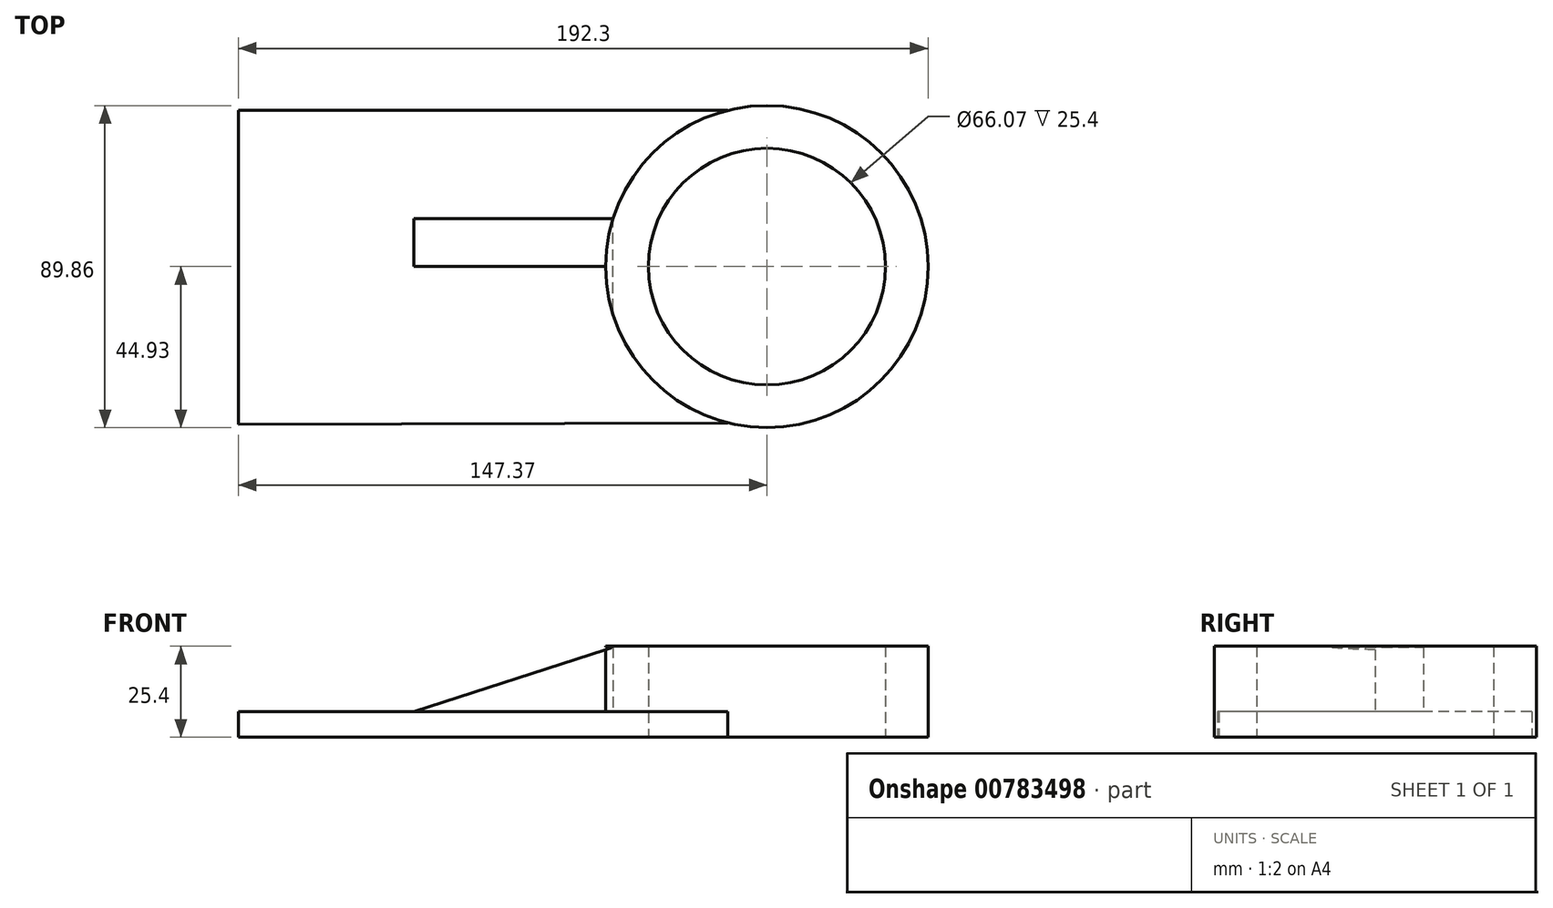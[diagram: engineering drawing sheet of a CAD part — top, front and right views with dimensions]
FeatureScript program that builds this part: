
annotation { "Feature Type Name" : "Feature", "Feature Type Description" : "" }
export const myFeature = defineFeature(function(context is Context, id is Id, definition is map)
    precondition{}
    {
        {
            var Q0;
            Q0=qCreatedBy(makeId("Top.planeOp"),FACE);
            var sketch = newSketch(context, id + "F0", { "sketchPlane" : qUnion([Q0])});
            skCircle(sketch, "E0", {"center": v(0, 0) * mm, "radius": 44.93 * mm});
            skLineSegment(sketch, "E1", {"start": v(-10.88, 43.59) * mm, "end": v(-147.37, 43.59) * mm});
            skLineSegment(sketch, "E2", {"start": v(-147.37, 43.59) * mm, "end": v(-147.37, -43.98) * mm});
            skLineSegment(sketch, "E3", {"start": v(-10.88, -43.59) * mm, "end": v(-147.37, -43.98) * mm});
            skCircle(sketch, "E4", {"center": v(0, 0) * mm, "radius": 33.03 * mm});
            skSolve(sketch);
        }
        {
            var Q0;
            {var subQ0=sQuery(id+"F0.wireOp",EDGE,"w4sub4mG-jCmE-7y8q-nihd-duvU38DYMYJ6");Q0=makeQuery(id+"F0.imprint","IMPRINT",FACE,{"disambiguationData":[TD([[makeQuery(id+"F0.imprint","IMPRINT",EDGE,{"derivedFrom":subQ0}),-1.0]])]});}
            var Q1;
            {var subQ0=sQuery(id+"F0.wireOp",EDGE,"w4sub4mG-jCmE-7y8q-nihd-duvU38DYMYJ6");Q1=makeQuery(id+"F0.imprint","IMPRINT",FACE,{"disambiguationData":[TD([[makeQuery(id+"F0.imprint","IMPRINT",EDGE,{"derivedFrom":subQ0}),1.0]])]});}
            var Q2;
            Q2=makeQuery(id+"F0.imprint","IMPRINT",FACE,{"disambiguationData":[TD([[makeQuery(id+"F0.imprint","IMPRINT",EDGE,{"derivedFrom":sQuery(id+"F0.wireOp",EDGE,"E4")}),-1.0]])]});
            extrude(context, id + "F1", {"entities" : qUnion([Q0, Q1, Q2]), "depth" : 25.4 * mm, "offsetDistance" : 25.4 * mm});
        }
        {
            var Q0;
            Q0 = qSketchRegion(id + "F0", true);
            extrude(context, id + "F2", {"entities" : qUnion([Q0]), "operationType" : NewBodyOperationType.ADD, "depth" : 7.11 * mm, "offsetDistance" : 25.4 * mm});
        }
        {
            var Q0;
            Q0=makeQuery(id+"F2.opExtrude","CAP_FACE",FACE,{"disambiguationData":[OSD([sQuery(id+"F0.wireOp",EDGE,"E0"),sQuery(id+"F0.wireOp",EDGE,"E1"),sQuery(id+"F0.wireOp",EDGE,"E2"),sQuery(id+"F0.wireOp",EDGE,"E3"),sQuery(id+"F0.wireOp",EDGE,"E4")])],"isStart":false});
            var sketch = newSketch(context, id + "F3", { "sketchPlane" : qUnion([Q0])});
            skLineSegment(sketch, "E5.bottom", {"start": v(-42.89, 13.39) * mm, "end": v(-98.37, 13.39) * mm});
            skLineSegment(sketch, "E5.top", {"start": v(-42.89, 0) * mm, "end": v(-98.37, 0) * mm});
            skLineSegment(sketch, "E5.left", {"start": v(-42.89, 13.39) * mm, "end": v(-42.89, 0) * mm});
            skLineSegment(sketch, "E5.right", {"start": v(-98.37, 13.39) * mm, "end": v(-98.37, 0) * mm});
            skSolve(sketch);
        }
        {
            var Q0;
            Q0 = qSketchRegion(id + "F3", true);
            extrude(context, id + "F4", {"entities" : qUnion([Q0]), "operationType" : NewBodyOperationType.ADD, "depth" : 18.03 * mm, "offsetDistance" : 25.4 * mm});
        }
        {
            var Q0;
            Q0=makeQuery(id+"F4.opExtrude","SWEPT_FACE",FACE,{"disambiguationData":[OSD([sQuery(id+"F3.wireOp",EDGE,"E5.bottom")])]});
            var sketch = newSketch(context, id + "F5", { "sketchPlane" : qUnion([Q0])});
            skLineSegment(sketch, "E6", {"start": v(98.37, 7.11) * mm, "end": v(42.89, 25.15) * mm});
            skSolve(sketch);
        }
        {
            var Q0;
            Q0=makeQuery(id+"F4.opExtrude","SWEPT_FACE",FACE,{"disambiguationData":[OSD([sQuery(id+"F3.wireOp",EDGE,"E5.right")])]});
            var sketch = newSketch(context, id + "F6", { "sketchPlane" : qUnion([Q0])});
            skLineSegment(sketch, "E7", {"start": v(-13.39, 7.11) * mm, "end": v(0, 7.11) * mm});
            skSolve(sketch);
        }
        {
            var Q0;
            Q0 = qSketchRegion(id + "F6", true);
            var Q1;
            Q1=makeQuery(id+"F5.imprint","IMPRINT",FACE,{"disambiguationData":[TD([[makeQuery(id+"F5.imprint","IMPRINT",EDGE,{"derivedFrom":sQuery(id+"F5.wireOp",EDGE,"E6")}),-1.0]])]});
            extrude(context, id + "F7", {"entities" : qUnion([Q0, Q1]), "operationType" : NewBodyOperationType.REMOVE, "oppositeDirection" : true, "depth" : 25.4 * mm, "offsetDistance" : 25.4 * mm});
        }
    });
